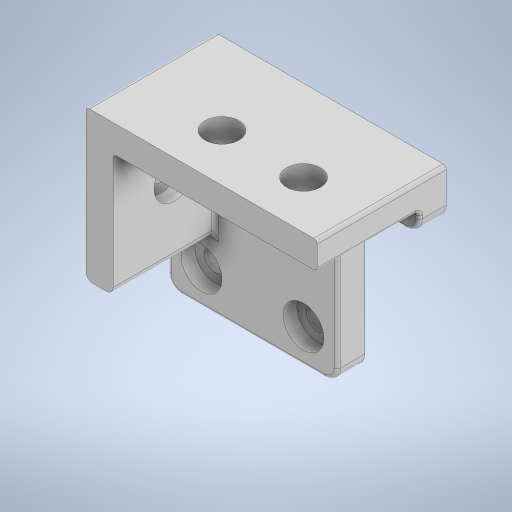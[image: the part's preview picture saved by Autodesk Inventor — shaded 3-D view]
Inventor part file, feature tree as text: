
AUTODESK INVENTOR PART (.ipt)
format: ipt  version: 2024.3 (Build 283343000, 343)  size: 479,744 bytes
history: native  units: mm
features: sketch x16, extrude x13, projected_geometry x7, fillet x4, hole x3, other x1
ambient origin geometry x8: Origin, YZ Plane, XZ Plane, XY Plane, X Axis, Y Axis, Z Axis, Center Point
bodies: Body1 (feature_tree)
feature tree (44):
  other  "ソリッド1"
  extrude  "押し出し1"  Depth=25.0mm
  hole  "穴1"  [1 undecoded]
  extrude  "押し出し2"  Depth=4.0mm TaperAngle=0.0deg
  extrude  "押し出し3"  Depth=15.0mm
  hole  "穴2"  [1 undecoded]
  extrude  "押し出し4"  Depth=5.0mm
  extrude  "押し出し5"  Depth=5.0mm
  extrude  "押し出し6"  Depth=3.0mm
  extrude  "押し出し7"  Depth=22.0mm TaperAngle=0.0deg
  extrude  "押し出し8"  Depth=4.0mm
  extrude  "押し出し9"  Depth=22.0mm TaperAngle=0.0deg
  extrude  "押し出し10"  Depth=10.5mm
  extrude  "押し出し11"  Depth=6.0mm
  hole  "穴4"  [1 undecoded]
  extrude  "押し出し12"  Depth=8.0mm
  extrude  "押し出し13"  Depth=6.0mm
  fillet  "フィレット1"  Radius=22.0mm
  fillet  "フィレット2"  Radius=3.0mm
  fillet  "フィレット3"  Radius=4.0mm
  fillet  "フィレット4"  Radius=3.0mm
  sketch  "スケッチ1"
  sketch  "スケッチ2"
  sketch  "スケッチ3"
  sketch  "スケッチ4"
  sketch  "スケッチ5"
  sketch  "スケッチ8"
  projected_geometry  "投影ループ1"
  sketch  "スケッチ9"
  sketch  "スケッチ10"
  projected_geometry  "投影ループ2"
  sketch  "スケッチ11"
  projected_geometry  "投影ループ3"
  sketch  "スケッチ12"
  projected_geometry  "投影ループ4"
  sketch  "スケッチ14"
  sketch  "スケッチ15"
  projected_geometry  "投影ループ5"
  sketch  "スケッチ16"
  projected_geometry  "投影ループ6"
  sketch  "スケッチ17"
  sketch  "スケッチ18"
  projected_geometry  "投影ループ7"
  sketch  "スケッチ19"
note: 3 required parameter values undecoded (feature->parameter linkage not recoverable at this tier; creation-order binding heuristic only, values carry confidence <= 0.55)
